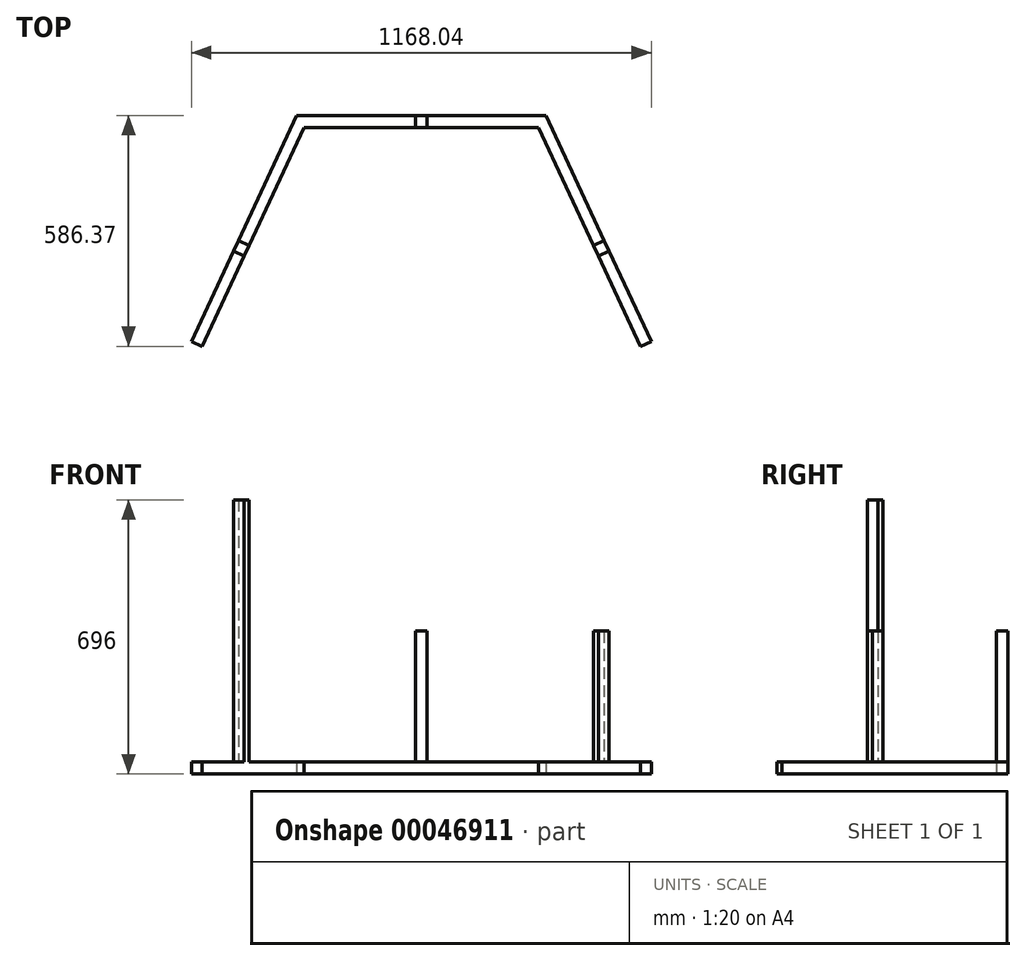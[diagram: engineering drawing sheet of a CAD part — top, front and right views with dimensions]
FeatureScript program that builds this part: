
annotation { "Feature Type Name" : "Feature", "Feature Type Description" : "" }
export const myFeature = defineFeature(function(context is Context, id is Id, definition is map)
    precondition{}
    {
        {
            var Q0;
            Q0=qCreatedBy(makeId("Top.planeOp"),FACE);
            var sketch = newSketch(context, id + "F0", { "sketchPlane" : qUnion([Q0])});
            skLineSegment(sketch, "E0", {"start": v(0, 0) * mm, "end": v(-297.39, 0) * mm});
            skLineSegment(sketch, "E1", {"start": v(-297.39, 0) * mm, "end": v(-556.83, -556.37) * mm});
            skLineSegment(sketch, "E2.0", {"start": v(-316.5, 30) * mm, "end": v(-584.02, -543.7) * mm});
            skLineSegment(sketch, "E2.1", {"start": v(0, 30) * mm, "end": v(-316.5, 30) * mm});
            skLineSegment(sketch, "E3", {"start": v(-584.02, -543.7) * mm, "end": v(-556.83, -556.37) * mm});
            skLineSegment(sketch, "E4.MirrorCS", {"start": v(316.5, 30) * mm, "end": v(584.02, -543.7) * mm});
            skLineSegment(sketch, "E5.MirrorCS", {"start": v(584.02, -543.7) * mm, "end": v(556.83, -556.37) * mm});
            skLineSegment(sketch, "E6.MirrorCS", {"start": v(297.39, 0) * mm, "end": v(556.83, -556.37) * mm});
            skLineSegment(sketch, "E7.MirrorCS", {"start": v(0, 0) * mm, "end": v(297.39, 0) * mm});
            skLineSegment(sketch, "E8.MirrorCS", {"start": v(0, 30) * mm, "end": v(316.5, 30) * mm});
            skSolve(sketch);
        }
        {
            var Q0;
            Q0 = qSketchRegion(id + "F0", true);
            extrude(context, id + "F1", {"entities" : qUnion([Q0]), "depth" : 30 * mm});
        }
        {
            var Q0;
            Q0=makeQuery(id+"F1.opExtrude","CAP_FACE",FACE,{"disambiguationData":[OSD([sQuery(id+"F0.wireOp",EDGE,"E0"),sQuery(id+"F0.wireOp",EDGE,"E1"),sQuery(id+"F0.wireOp",EDGE,"E2.0"),sQuery(id+"F0.wireOp",EDGE,"E2.1"),sQuery(id+"F0.wireOp",EDGE,"E3"),sQuery(id+"F0.wireOp",EDGE,"E4.MirrorCS"),sQuery(id+"F0.wireOp",EDGE,"E5.MirrorCS"),sQuery(id+"F0.wireOp",EDGE,"E6.MirrorCS"),sQuery(id+"F0.wireOp",EDGE,"E7.MirrorCS"),sQuery(id+"F0.wireOp",EDGE,"E8.MirrorCS")])],"isStart":false});
            var sketch = newSketch(context, id + "F2", { "sketchPlane" : qUnion([Q0])});
            skLineSegment(sketch, "E9", {"start": v(0, 0) * mm, "end": v(15, 0) * mm});
            skLineSegment(sketch, "E10", {"start": v(15, 0) * mm, "end": v(15, 30) * mm});
            skLineSegment(sketch, "E11", {"start": v(15, 30) * mm, "end": v(-15, 30) * mm});
            skLineSegment(sketch, "E12", {"start": v(-15, 30) * mm, "end": v(-15, 0) * mm});
            skLineSegment(sketch, "E13", {"start": v(-15, 0) * mm, "end": v(0, 0) * mm});
            skSolve(sketch);
        }
        {
            var Q0;
            Q0 = qSketchRegion(id + "F2", true);
            extrude(context, id + "F3", {"entities" : qUnion([Q0]), "depth" : 333 * mm});
        }
        {
            var Q0;
            {var subQ0=sQuery(id+"F0.wireOp",EDGE,"E0");var subQ1=sQuery(id+"F0.wireOp",EDGE,"E1");var subQ2=sQuery(id+"F0.wireOp",EDGE,"E2.0");var subQ3=sQuery(id+"F0.wireOp",EDGE,"E2.1");var subQ4=sQuery(id+"F0.wireOp",EDGE,"E3");var subQ5=sQuery(id+"F0.wireOp",EDGE,"E7.MirrorCS");var subQ6=sQuery(id+"F0.wireOp",EDGE,"E8.MirrorCS");Q0=makeQuery(id+"F3.boolean.opBoolean","SPLIT",FACE,{"disambiguationData":[TD([makeQuery(id+"F1.opExtrude","SWEPT_FACE",FACE,{"disambiguationData":[OSD([subQ1])]})])],"derivedFrom":makeQuery(id+"F1.opExtrude","CAP_FACE",FACE,{"disambiguationData":[OSD([subQ0,subQ1,subQ2,subQ3,subQ4,sQuery(id+"F0.wireOp",EDGE,"E4.MirrorCS"),sQuery(id+"F0.wireOp",EDGE,"E5.MirrorCS"),sQuery(id+"F0.wireOp",EDGE,"E6.MirrorCS"),subQ5,subQ6])],"isStart":false})});}
            var sketch = newSketch(context, id + "F4", { "sketchPlane" : qUnion([Q0])});
            skLineSegment(sketch, "E14", {"start": v(-464.42, -287.2) * mm, "end": v(-437.23, -299.89) * mm});
            skLineSegment(sketch, "E15", {"start": v(-437.23, -299.89) * mm, "end": v(-449.9, -327.08) * mm});
            skLineSegment(sketch, "E16", {"start": v(-449.9, -327.08) * mm, "end": v(-477.1, -314.4) * mm});
            skLineSegment(sketch, "E17", {"start": v(-477.1, -314.4) * mm, "end": v(-464.42, -287.2) * mm});
            skSolve(sketch);
        }
        {
            var Q0;
            Q0 = qSketchRegion(id + "F4", true);
            extrude(context, id + "F5", {"entities" : qUnion([Q0]), "depth" : 333 * mm});
        }
        {
            var Q0;
            Q0=makeQuery(id+"F5.opExtrude","SWEPT_BODY",BODY,{"disambiguationData":[OSD([sQuery(id+"F4.wireOp",EDGE,"E14"),sQuery(id+"F4.wireOp",EDGE,"E15"),sQuery(id+"F4.wireOp",EDGE,"E16"),sQuery(id+"F4.wireOp",EDGE,"E17")])]});
            var Q1;
            Q1=qCreatedBy(makeId("Right.planeOp"),FACE);
            mirror(context, id + "F6", {"entities" : qUnion([Q0]), "mirrorPlane" : qUnion([Q1])});
        }
        {
            var Q0;
            Q0=makeQuery(id+"F5.opExtrude","SWEPT_BODY",BODY,{"disambiguationData":[OSD([sQuery(id+"F4.wireOp",EDGE,"E14"),sQuery(id+"F4.wireOp",EDGE,"E15"),sQuery(id+"F4.wireOp",EDGE,"E16"),sQuery(id+"F4.wireOp",EDGE,"E17")])]});
            var Q1;
            Q1=makeQuery(id+"F3.opExtrude","CAP_FACE",FACE,{"disambiguationData":[OSD([sQuery(id+"F2.wireOp",EDGE,"E9"),sQuery(id+"F2.wireOp",EDGE,"E10"),sQuery(id+"F2.wireOp",EDGE,"E11"),sQuery(id+"F2.wireOp",EDGE,"E12"),sQuery(id+"F2.wireOp",EDGE,"E13")])],"isStart":false});
            mirror(context, id + "F7", {"operationType" : NewBodyOperationType.ADD, "entities" : qUnion([Q0]), "mirrorPlane" : qUnion([Q1])});
        }
    });
